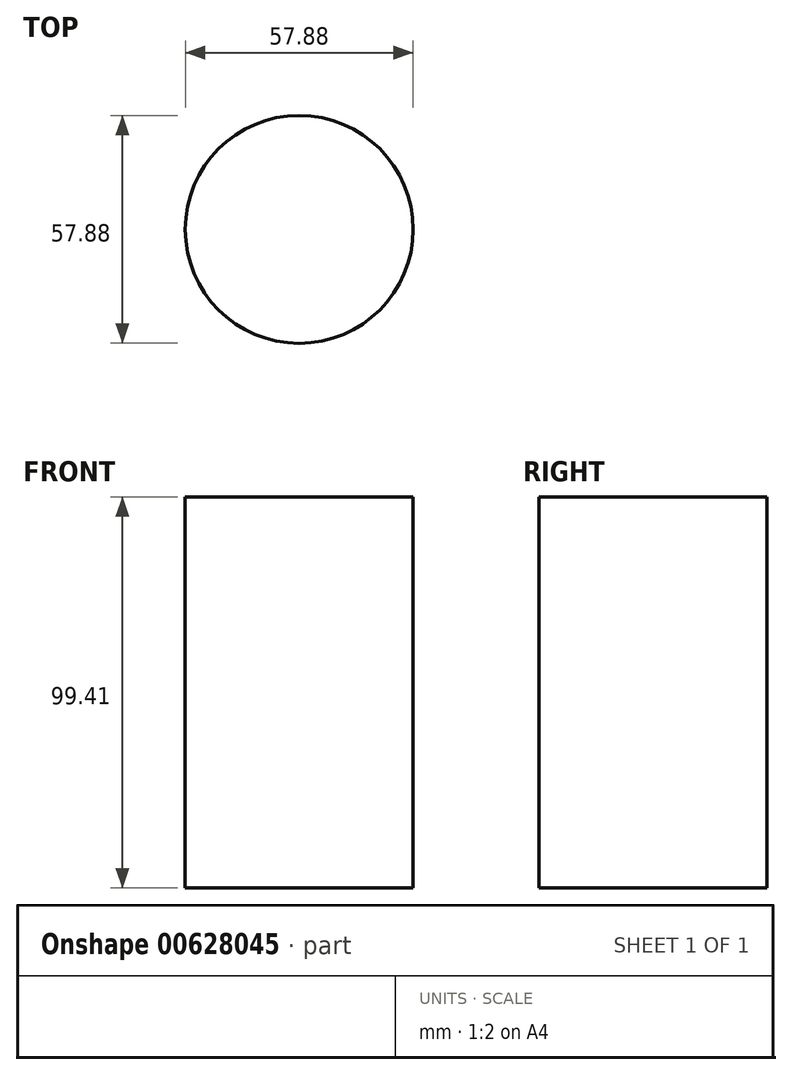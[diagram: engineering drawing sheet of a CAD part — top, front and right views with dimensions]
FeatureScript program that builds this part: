
annotation { "Feature Type Name" : "Feature", "Feature Type Description" : "" }
export const myFeature = defineFeature(function(context is Context, id is Id, definition is map)
    precondition{}
    {
        {
            var Q0;
            Q0=qCreatedBy(makeId("Front.planeOp"),FACE);
            var sketch = newSketch(context, id + "F0", { "sketchPlane" : qUnion([Q0])});
            skLineSegment(sketch, "E0", {"start": v(-28.94, 41.07) * mm, "end": v(-28.94, -58.34) * mm});
            skLineSegment(sketch, "E1", {"start": v(-28.94, 41.07) * mm, "end": v(0, 41.07) * mm});
            skLineSegment(sketch, "E2", {"start": v(-28.94, -58.34) * mm, "end": v(0, -58.34) * mm});
            skLineSegment(sketch, "E3", {"start": v(0, 41.07) * mm, "end": v(0, -58.34) * mm, "construction": true});
            skSolve(sketch);
        }
        {
            var Q0;
            Q0 = qSketchRegion(id + "F0", true);
            var Q1;
            Q1=sQuery(id+"F0.wireOp",EDGE,"E1");
            var Q2;
            Q2=sQuery(id+"F0.wireOp",EDGE,"E0");
            var Q3;
            Q3=sQuery(id+"F0.wireOp",EDGE,"E2");
            var Q4;
            Q4=sQuery(id+"F0.wireOp",EDGE,"E3");
            revolve(context, id + "F1", {"bodyType" : ToolBodyType.SURFACE, "entities" : qUnion([Q0]), "surfaceEntities" : qUnion([Q1, Q2, Q3]), "axis" : qUnion([Q4]), "revolveType" : RevolveType.FULL});
        }
    });
